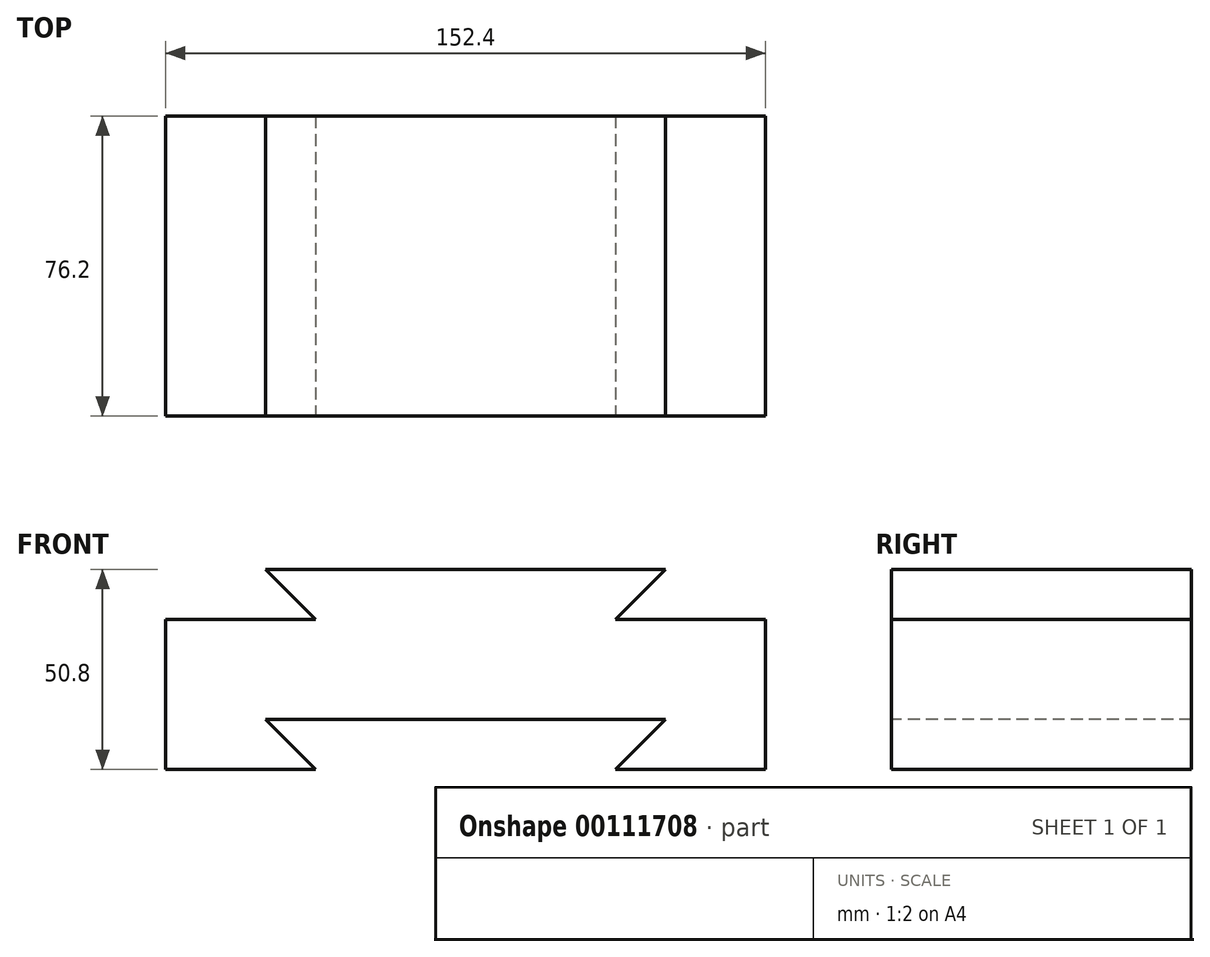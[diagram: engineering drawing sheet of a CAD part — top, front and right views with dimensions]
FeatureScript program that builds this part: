
annotation { "Feature Type Name" : "Feature", "Feature Type Description" : "" }
export const myFeature = defineFeature(function(context is Context, id is Id, definition is map)
    precondition{}
    {
        {
            var Q0;
            Q0=qCreatedBy(makeId("Top.planeOp"),FACE);
            var sketch = newSketch(context, id + "F0", { "sketchPlane" : qUnion([Q0])});
            skLineSegment(sketch, "E0.bottom", {"start": v(76.2, 38.1) * mm, "end": v(-76.2, 38.1) * mm});
            skLineSegment(sketch, "E0.top", {"start": v(76.2, -38.1) * mm, "end": v(-76.2, -38.1) * mm});
            skLineSegment(sketch, "E0.left", {"start": v(76.2, 38.1) * mm, "end": v(76.2, -38.1) * mm});
            skLineSegment(sketch, "E0.right", {"start": v(-76.2, 38.1) * mm, "end": v(-76.2, -38.1) * mm});
            skPoint(sketch, "E0.middle", {"position": v(0, 0) * mm});
            skSolve(sketch);
        }
        {
            var Q0;
            Q0 = qSketchRegion(id + "F60At8kws3Clvms_0", true);
            var Q1;
            Q1=makeQuery(id+"F0.imprint","IMPRINT",FACE,{"disambiguationData":[TD([[makeQuery(id+"F0.imprint","IMPRINT",EDGE,{"derivedFrom":sQuery(id+"F0.wireOp",EDGE,"E0.bottom")}),1.0]])]});
            extrude(context, id + "F1", {"entities" : qUnion([Q0, Q1]), "depth" : 50.8 * mm});
        }
        {
            var Q0;
            Q0=makeQuery(id+"F1.opExtrude","SWEPT_FACE",FACE,{"disambiguationData":[OSD([sQuery(id+"F0.wireOp",EDGE,"E0.top")])]});
            var sketch = newSketch(context, id + "F2", { "sketchPlane" : qUnion([Q0])});
            skLineSegment(sketch, "E1", {"start": v(0, 0) * mm, "end": v(38.1, 0) * mm});
            skLineSegment(sketch, "E2", {"start": v(0, 0) * mm, "end": v(-38.1, 0) * mm});
            skLineSegment(sketch, "E3", {"start": v(0, 0) * mm, "end": v(0, 12.7) * mm});
            skLineSegment(sketch, "E4", {"start": v(0, 12.7) * mm, "end": v(50.8, 12.7) * mm});
            skLineSegment(sketch, "E5", {"start": v(0, 12.7) * mm, "end": v(-50.8, 12.7) * mm});
            skLineSegment(sketch, "E6", {"start": v(-50.8, 12.7) * mm, "end": v(-38.1, 0) * mm});
            skLineSegment(sketch, "E7", {"start": v(38.1, 0) * mm, "end": v(50.8, 12.7) * mm});
            skSolve(sketch);
        }
        {
            var Q0;
            Q0=makeQuery(id+"F2.imprint","IMPRINT",FACE,{"disambiguationData":[TD([[makeQuery(id+"F2.imprint","IMPRINT",EDGE,{"derivedFrom":sQuery(id+"F2.wireOp",EDGE,"E2")}),-1.0]])]});
            extrude(context, id + "F3", {"entities" : qUnion([Q0]), "operationType" : NewBodyOperationType.REMOVE, "endBound" : BoundingType.THROUGH_ALL, "oppositeDirection" : true, "depth" : 25.4 * mm});
        }
        {
            var Q0;
            Q0=makeQuery(id+"F2.imprint","IMPRINT",FACE,{"disambiguationData":[TD([[makeQuery(id+"F2.imprint","IMPRINT",EDGE,{"derivedFrom":sQuery(id+"F2.wireOp",EDGE,"E1")}),-1.0]])]});
            extrude(context, id + "F4", {"entities" : qUnion([Q0]), "operationType" : NewBodyOperationType.REMOVE, "endBound" : BoundingType.THROUGH_ALL, "oppositeDirection" : true, "depth" : 25.4 * mm});
        }
        {
            var Q0;
            Q0=makeQuery(id+"F2.imprint","IMPRINT",FACE,{"disambiguationData":[TD([[makeQuery(id+"F2.imprint","IMPRINT",EDGE,{"derivedFrom":sQuery(id+"F2.wireOp",EDGE,"E4")}),1.0]])]});
            var sketch = newSketch(context, id + "F5", { "sketchPlane" : qUnion([Q0])});
            skLineSegment(sketch, "E8", {"start": v(-38.1, 38.1) * mm, "end": v(-76.2, 38.1) * mm});
            skLineSegment(sketch, "E9", {"start": v(-50.8, 50.8) * mm, "end": v(-38.1, 38.1) * mm});
            skLineSegment(sketch, "E10", {"start": v(-76.2, 38.1) * mm, "end": v(-76.2, 50.8) * mm});
            skLineSegment(sketch, "E11", {"start": v(-76.2, 50.8) * mm, "end": v(-50.8, 50.8) * mm});
            skSolve(sketch);
        }
        {
            var Q0;
            Q0 = qSketchRegion(id + "F5", true);
            extrude(context, id + "F6", {"entities" : qUnion([Q0]), "operationType" : NewBodyOperationType.REMOVE, "endBound" : BoundingType.THROUGH_ALL, "oppositeDirection" : true, "depth" : 25.4 * mm});
        }
        {
            var Q0;
            Q0=makeQuery(id+"F2.imprint","IMPRINT",FACE,{"disambiguationData":[TD([[makeQuery(id+"F2.imprint","IMPRINT",EDGE,{"derivedFrom":sQuery(id+"F2.wireOp",EDGE,"E4")}),1.0]])]});
            var sketch = newSketch(context, id + "F7", { "sketchPlane" : qUnion([Q0])});
            skLineSegment(sketch, "E12", {"start": v(38.1, 38.1) * mm, "end": v(76.2, 38.1) * mm});
            skLineSegment(sketch, "E13", {"start": v(76.2, 38.1) * mm, "end": v(76.2, 50.8) * mm});
            skLineSegment(sketch, "E14", {"start": v(76.2, 50.8) * mm, "end": v(50.8, 50.8) * mm});
            skLineSegment(sketch, "E15", {"start": v(38.1, 38.1) * mm, "end": v(50.8, 50.8) * mm});
            skSolve(sketch);
        }
        {
            var Q0;
            Q0 = qSketchRegion(id + "F7", true);
            extrude(context, id + "F8", {"entities" : qUnion([Q0]), "operationType" : NewBodyOperationType.REMOVE, "endBound" : BoundingType.THROUGH_ALL, "oppositeDirection" : true, "depth" : 25.4 * mm});
        }
    });
